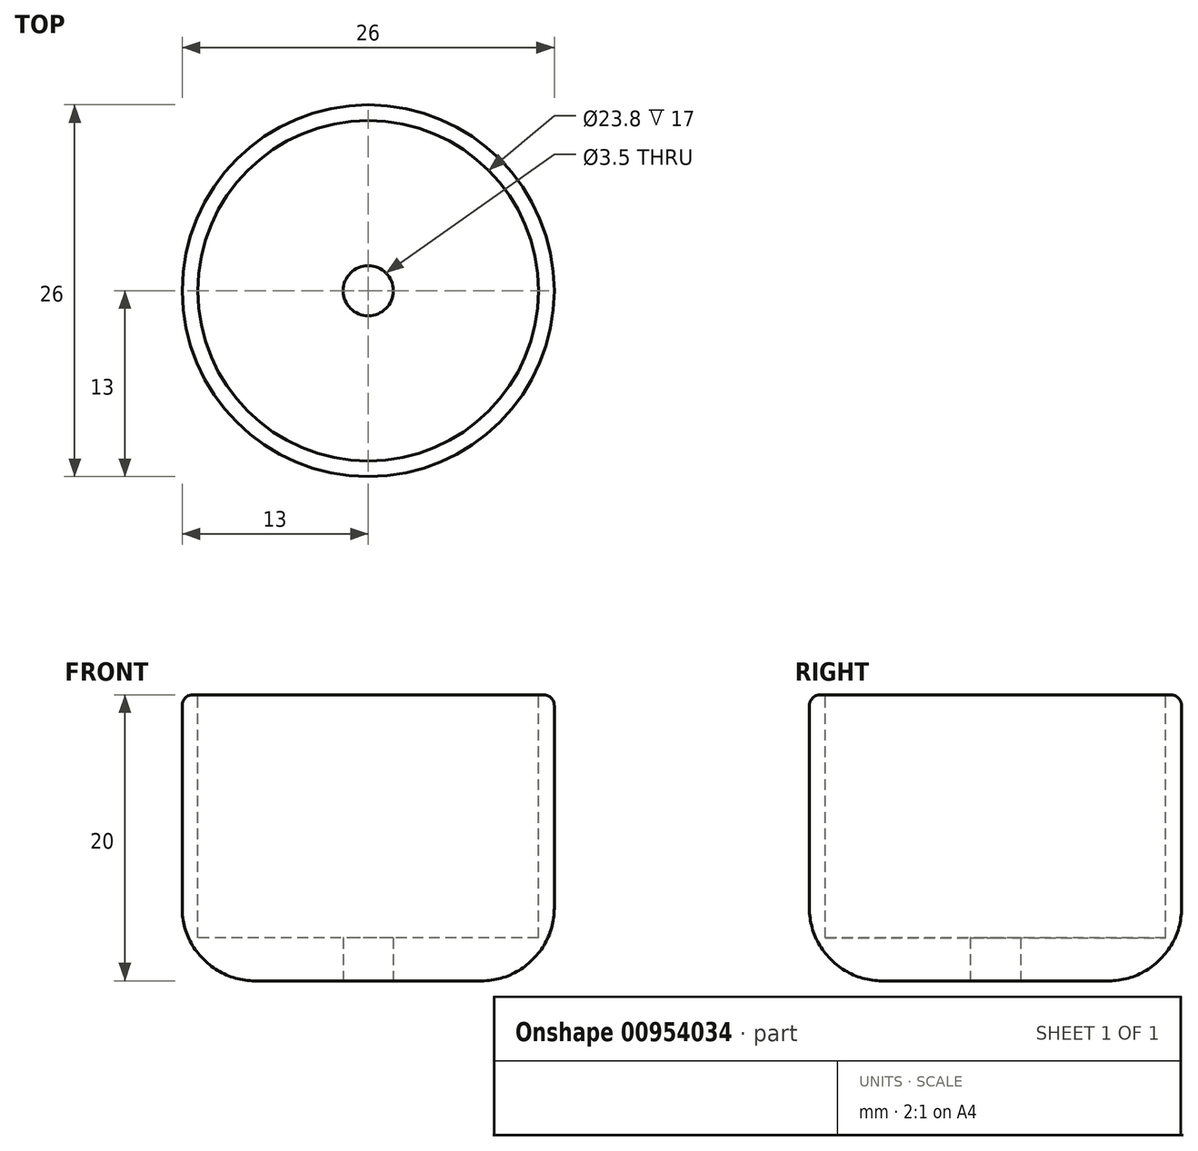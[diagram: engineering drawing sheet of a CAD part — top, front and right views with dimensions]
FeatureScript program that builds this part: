
annotation { "Feature Type Name" : "Feature", "Feature Type Description" : "" }
export const myFeature = defineFeature(function(context is Context, id is Id, definition is map)
    precondition{}
    {
        {
            var Q0;
            Q0=qCreatedBy(makeId("Top.planeOp"),FACE);
            var sketch = newSketch(context, id + "F0", { "sketchPlane" : qUnion([Q0])});
            skCircle(sketch, "E0", {"center": v(0, 0) * mm, "radius": 13 * mm});
            skSolve(sketch);
        }
        {
            var Q0;
            Q0=makeQuery(id+"F0.imprint","IMPRINT",FACE,{"disambiguationData":[TD([[makeQuery(id+"F0.imprint","IMPRINT",EDGE,{"derivedFrom":sQuery(id+"F0.wireOp",EDGE,"E0")}),1.0]])]});
            extrude(context, id + "F1", {"entities" : qUnion([Q0]), "depth" : 20 * mm, "offsetDistance" : 25 * mm});
        }
        {
            var Q0;
            Q0=makeQuery(id+"F1.opExtrude","CAP_FACE",FACE,{"disambiguationData":[OSD([sQuery(id+"F0.wireOp",EDGE,"E0")])],"isStart":false});
            var sketch = newSketch(context, id + "F2", { "sketchPlane" : qUnion([Q0])});
            skCircle(sketch, "E1", {"center": v(0, 0) * mm, "radius": 11.9 * mm});
            skSolve(sketch);
        }
        {
            var Q0;
            Q0=makeQuery(id+"F2.imprint","IMPRINT",FACE,{"disambiguationData":[TD([[makeQuery(id+"F2.imprint","IMPRINT",EDGE,{"derivedFrom":sQuery(id+"F2.wireOp",EDGE,"E1")}),1.0]])]});
            extrude(context, id + "F3", {"entities" : qUnion([Q0]), "operationType" : NewBodyOperationType.REMOVE, "oppositeDirection" : true, "depth" : 17 * mm, "offsetDistance" : 25 * mm});
        }
        {
            var Q0;
            Q0=qCreatedBy(makeId("Top.planeOp"),FACE);
            var sketch = newSketch(context, id + "F4", { "sketchPlane" : qUnion([Q0])});
            skCircle(sketch, "E2", {"center": v(0, 0) * mm, "radius": 1.75 * mm});
            skSolve(sketch);
        }
        {
            var Q0;
            Q0 = qSketchRegion(id + "F4", true);
            extrude(context, id + "F5", {"entities" : qUnion([Q0]), "operationType" : NewBodyOperationType.REMOVE, "depth" : 4.1 * mm, "offsetDistance" : 25 * mm});
        }
        {
            var Q0;
            Q0=makeQuery(id+"F1.opExtrude","CAP_EDGE",EDGE,{"disambiguationData":[OSD([sQuery(id+"F0.wireOp",EDGE,"E0")])],"isStart":true});
            chamfer(context, id + "F6", {"entities" : qUnion([Q0]), "width" : 3 * mm, "tangentPropagation" : true});
        }
        {
            var Q0;
            {var subQ0=sQuery(id+"F0.wireOp",EDGE,"E0");Q0=makeQuery(id+"F6.opChamfer","BLEND_EDGE",EDGE,{"blendedFrom":[makeQuery(id+"F1.opExtrude","CAP_EDGE",EDGE,{"disambiguationData":[OSD([subQ0])],"isStart":true}),makeQuery(id+"F1.opExtrude","CAP_FACE",FACE,{"disambiguationData":[OSD([subQ0])],"isStart":true})],"blendedInto":[makeQuery(id+"F1.opExtrude","CAP_FACE",FACE,{"disambiguationData":[OSD([subQ0])],"isStart":true})]});}
            var Q1;
            {var subQ0=sQuery(id+"F0.wireOp",EDGE,"E0");Q1=makeQuery(id+"F6.opChamfer","BLEND_EDGE",EDGE,{"blendedFrom":[makeQuery(id+"F1.opExtrude","CAP_EDGE",EDGE,{"disambiguationData":[OSD([subQ0])],"isStart":true}),makeQuery(id+"F1.opExtrude","SWEPT_FACE",FACE,{"disambiguationData":[OSD([subQ0])]})],"blendedInto":[makeQuery(id+"F1.opExtrude","SWEPT_FACE",FACE,{"disambiguationData":[OSD([subQ0])]})]});}
            fillet(context, id + "F7", {"entities" : qUnion([Q0, Q1]), "radius" : 5 * mm, "tangentPropagation" : true, "allowEdgeOverflow" : false});
        }
        {
            var Q0;
            Q0=makeQuery(id+"F1.opExtrude","CAP_EDGE",EDGE,{"disambiguationData":[OSD([sQuery(id+"F0.wireOp",EDGE,"E0")])],"isStart":false});
            fillet(context, id + "F8", {"entities" : qUnion([Q0]), "radius" : .75 * mm, "tangentPropagation" : true, "allowEdgeOverflow" : false});
        }
    });
